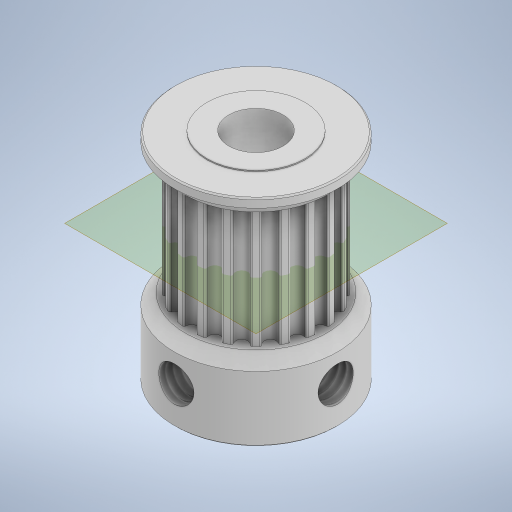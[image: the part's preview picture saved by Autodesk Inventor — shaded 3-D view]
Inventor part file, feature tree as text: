
AUTODESK INVENTOR PART (.ipt)
format: ipt  version: 2024 (Build 280153000, 153)  size: 453,120 bytes
history: native  units: mm
features: plane x4, extrude x2, mirror x2, chamfer x2, projected_geometry x2, revolve x1, hole x1, pattern_circular x1
ambient origin geometry x8: Origin, YZ Plane, XZ Plane, XY Plane, X Axis, Y Axis, Z Axis, Center Point
bodies: Solid1 (feature_tree)
feature tree (15):
  revolve  "Revolution1"  [1 undecoded]
  extrude  "Extrusion1"  Depth=2.5mm
  plane  "Work Plane1"
  mirror  "Mirror1"
  chamfer  "Chamfer2"  Distance=20.0mm
  chamfer  "Chamfer1"  Distance=11.0mm
  plane  "Work Plane2"
  hole  "Hole1"  [1 undecoded]
  plane  "Work Plane3"
  mirror  "Mirror2"
  extrude  "Extrusion2"  Depth=6.11mm
  pattern_circular  "Circular Pattern1"  Angle=90.0deg  [1 undecoded]
  plane  "Work Plane4"
  projected_geometry  "Projected Loop1"
  projected_geometry  "Project Cut Edges2"
note: 3 required parameter values undecoded (feature->parameter linkage not recoverable at this tier; creation-order binding heuristic only, values carry confidence <= 0.55)